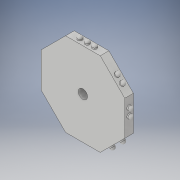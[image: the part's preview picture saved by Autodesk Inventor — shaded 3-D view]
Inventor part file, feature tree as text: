
AUTODESK INVENTOR PART (.ipt)
format: ipt  version: 2017 (Build 210142000, 142)  size: 351,744 bytes
history: native  units: in
note: dims shown in document units (in); Inventor stores cm internally (conversion verified against a paired STEP export)
features: sketch x11, extrude x10, fillet x7, pattern_circular x1
ambient origin geometry x8: Origin, YZ Plane, XZ Plane, XY Plane, X Axis, Y Axis, Z Axis, Center Point
bodies: Solid1 (feature_tree)
feature tree (29):
  extrude  "Extrusion1"  Depth=0.1181in TaperAngle=0.0deg
  extrude  "Extrusion2"  Depth=0.063in
  fillet  "Fillet1"  Radius=0.1in
  sketch  "Sketch3"  dims[d8=0.063in d9=0.063in d10=0.059in]
  sketch  "Sketch4"  dims[d11=0.0472in d12=0.0in d13=0.0315in d24=0.059in]
  sketch  "Sketch5"  dims[d25=0.063in d26=0.1in d27=0.1in d28=0.063in d29=0.063in d31=0.0575in d32=0.059in d34=0.0in d35=0.059in]
  sketch  "Sketch6"  dims[d36=0.059in]
  sketch  "Sketch7"  dims[d40=0.063in d41=0.1in d42=0.1in d43=0.063in d44=0.063in d46=0.059in d47=0.0in d48=0.059in d49=0.059in d50=0.0in d51=0.0in]
  sketch  "Sketch8"  dims[d70=0.063in d71=0.1in d72=0.1in d73=0.063in d74=0.063in d76=0.059in d77=0.0in d78=0.059in d79=0.059in d81=0.0in d82=0.0in]
  sketch  "Sketch9"  dims[d83=0.063in d84=0.1in d85=0.1in d86=0.063in d87=0.063in d89=0.059in d90=0.059in d91=0.059in d92=0.0in d93=0.0in d94=0.0in d95=0.0in]
  extrude  "Extrusion6"  Depth=0.063in
  fillet  "Fillet5"  Radius=0.059in
  extrude  "Extrusion7"  Depth=0.0315in
  fillet  "Fillet6"  Radius=0.059in
  extrude  "Extrusion8"  TaperAngle=0.0deg  [1 undecoded]
  fillet  "Fillet7"  Radius=0.059in
  extrude  "Extrusion9"  TaperAngle=0.0deg  [1 undecoded]
  fillet  "Fillet8"  [1 undecoded]
  extrude  "Extrusion10"  TaperAngle=0.0deg  [1 undecoded]
  fillet  "Fillet9"  [1 undecoded]
  extrude  "Extrusion11"  TaperAngle=0.0deg  [1 undecoded]
  fillet  "Fillet10"  [1 undecoded]
  extrude  "Extrusion14"  Depth=0.0315in
  pattern_circular  "Circular Pattern4"  [2 undecoded]
  extrude  "Extrusion15"  Depth=0.0315in
  sketch  "Sketch1"  dims[d2=0.4724in d3=0.1181in d4=0.0in]
  sketch  "Sketch2"  dims[d5=0.063in d6=0.1in d7=0.1in]
  sketch  "Sketch11"  dims[d96=0.063in d97=0.1in d98=0.1in d99=0.063in d100=0.063in d102=0.059in d103=0.059in d104=0.059in d105=0.0in d106=0.0in d107=0.0in d108=0.0in]
  sketch  "Sketch12"  dims[d109=0.063in d110=0.1in d111=0.1in d112=0.063in d113=0.063in d115=0.059in d116=0.059in d117=0.059in d118=0.0in d119=0.0in d120=0.0in d121=0.0in d122=0.0472in d123=0.0in d124=0.0315in d125=0.0472in d126=0.0in d127=0.0315in d128=0.0472in d129=0.0in d130=0.0315in d131=0.0472in d132=0.0in d133=0.0315in d134=0.0472in d135=0.0in d136=0.0315in d137=0.0472in d138=0.0in d139=0.0315in d148=0.6in d154=12.5984in d156=360.0deg d161=0.04in d162=0.04in d163=0.1931in d164=0.0in d165=3.1496in d166=360.0deg d168=0.075in d169=0.236in d170=0.236in d171=0.236in d172=0.236in d173=0.236in d175=0.236in d176=0.236in d177=0.126in d178=1.0in d179=0.0in]
note: 9 required parameter values undecoded (feature->parameter linkage not recoverable at this tier; creation-order binding heuristic only, values carry confidence <= 0.55)
